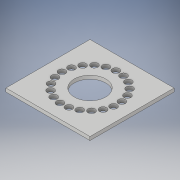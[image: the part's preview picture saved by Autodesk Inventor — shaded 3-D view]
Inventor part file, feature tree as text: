
AUTODESK INVENTOR PART (.ipt)
format: ipt  version: 2019 (Build 230136000, 136)  size: 153,600 bytes
history: native  units: in
note: dims shown in document units (in); Inventor stores cm internally (conversion verified against a paired STEP export)
features: extrude x1, sketch x1
ambient origin geometry x8: Origin, YZ Plane, XZ Plane, XY Plane, X Axis, Y Axis, Z Axis, Center Point
bodies: Solid1 (feature_tree)
feature tree (2):
  extrude  "Extrusion1"  Depth=0.125in
  sketch  "Sketch1"  dims[d0=2.0in d1=0.25in d6=3.0in d7=3.0in d8=0.125in d9=0.0in d13=8.2677in d15=360.0deg d17=1.122in]
